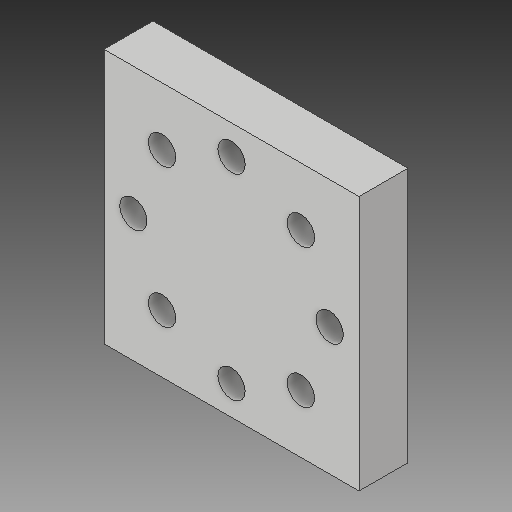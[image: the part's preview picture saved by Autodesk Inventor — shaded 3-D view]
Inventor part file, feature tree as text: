
AUTODESK INVENTOR PART (.ipt)
format: ipt  version: 2017 (Build 210142000, 142)  size: 118,272 bytes
history: native  units: in
note: dims shown in document units (in); Inventor stores cm internally (conversion verified against a paired STEP export)
features: sketch x3, extrude x1, hole x1
ambient origin geometry x8: Origin, YZ Plane, XZ Plane, XY Plane, X Axis, Y Axis, Z Axis, Center Point
bodies: Solid1 (feature_tree)
feature tree (5):
  extrude  "Extrusion1"  Depth=1.0in
  hole  "Hole1"  [1 undecoded]
  sketch  "Sketch3"  dims[d5=0.385in d6=0.107in d7=0.75in d8=0.375in d9=0.25in d10=0.5635in d11=1.0in d12=0.8108in d13=3.1496in d15=360.0deg]
  sketch  "Sketch1"  dims[d0=1.0in d1=1.0in]
  sketch  "Sketch2"  dims[d2=0.192in d3=0.0in d4=0.5in]
note: 1 required parameter value undecoded (feature->parameter linkage not recoverable at this tier; creation-order binding heuristic only, values carry confidence <= 0.55)
